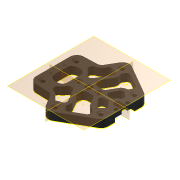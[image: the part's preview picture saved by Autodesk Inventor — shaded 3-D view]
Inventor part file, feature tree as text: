
AUTODESK INVENTOR PART (.ipt)
format: ipt  version: 2016 (Build 200138000, 138)  size: 927,744 bytes
history: native  units: mm
features: sketch x17, extrude x15, plane x3, pattern_circular x3, projected_geometry x3, thread x2, reference x2, chamfer x1, revolve x1, fillet x1
ambient origin geometry x8: Origin, YZ Plane, XZ Plane, XY Plane, X Axis, Y Axis, Z Axis, Center Point
bodies: Solid1 (feature_tree)
feature tree (48):
  extrude  "Extrusion1"  Depth=10.0mm
  extrude  "Extrusion2"  Depth=10.0mm
  extrude  "Extrusion4"  Depth=10.0mm
  chamfer  "Chamfer1"  Distance=8.0mm
  plane  "Work Plane2"
  extrude  "Extrusion10"  Depth=8.0mm TaperAngle=0.0deg
  plane  "Work Plane8"
  extrude  "Extrusion17"  Depth=4.0mm
  extrude  "Extrusion21"  Depth=4.0mm
  extrude  "Extrusion27"  Depth=4.0mm
  extrude  "Extrusion28"  Depth=3.0mm
  extrude  "Extrusion29"  Depth=2.0mm
  plane  "Work Plane10"
  revolve  "Revolution2"  [1 undecoded]
  pattern_circular  "Circular Pattern3"  [2 undecoded]
  thread  "Thread3"  [1 undecoded]
  thread  "Thread4"  [1 undecoded]
  extrude  "Extrusion31"  Depth=4.0mm
  extrude  "Extrusion33"  Depth=10.0mm TaperAngle=0.0deg
  extrude  "Extrusion34"  Depth=8.0mm
  extrude  "Extrusion35"  Depth=8.0mm
  fillet  "Fillet8"  Radius=4.0mm
  extrude  "Extrusion36"  Depth=0.05mm
  extrude  "Extrusion37"  Depth=0.05mm
  pattern_circular  "Circular Pattern6"  [2 undecoded]
  pattern_circular  "Circular Pattern7"  [2 undecoded]
  sketch  "Sketch47"  dims[d133=6.0mm d134=7.5mm d135=8.0mm d136=0.0mm d175=4.0mm d176=4.0mm d177=10.0mm d178=0.0mm d179=8.0mm d180=8.0mm d181=4.0mm d182=0.0mm d183=2.4mm d184=2.4mm d185=8.0mm d186=0.0mm d205=3.5mm d206=10.0mm d207=90.0deg d208=60.0mm d209=360.0deg d211=10.0mm d212=0.0mm d213=10.0mm d214=0.0mm d215=6.0mm d216=6.0mm d217=1.0mm d218=0.0mm d232=8.0mm d233=0.0mm d234=0.349066mm d235=0.349066mm d236=60.0deg d237=60.0deg d238=5.0mm d239=8.0mm d240=0.0mm d243=5.0mm d244=6.0mm d247=3.5mm d248=3.5mm d249=8.0mm d250=8.0mm d251=8.0mm d252=14.0mm d253=8.0mm d254=3.5mm d255=1.75mm d256=6.0mm d260=3.5mm d261=3.5mm d262=3.5mm d263=6.0mm d264=6.0mm d265=6.0mm d266=6.0mm d267=10.0mm d268=10.0mm d269=17.5mm d270=17.5mm d271=3.5mm d272=3.5mm d273=6.0mm d274=6.0mm d275=6.0mm d276=6.0mm d277=3.0mm d279=8.0mm d280=0.0mm d281=3.0mm d282=3.0mm d283=3.0mm d284=0.9mm d285=0.9mm d286=3.6mm d287=3.6mm d288=10.0mm d289=0.0mm d290=10.0mm d291=0.0mm d292=30.0mm d293=360.0deg d295=60.0mm d296=360.0deg d298=0.05mm]
  sketch  "Sketch1"  dims[d1=10.0mm d2=10.0mm]
  reference  "Reference1"
  sketch  "Sketch2"  dims[d3=10.0mm d4=10.0mm]
  reference  "Reference4"
  sketch  "Sketch4"  dims[d5=10.0mm d6=10.0mm d9=8.0mm d10=0.0mm]
  sketch  "Sketch14"  dims[d14=6.5mm d15=8.0mm d16=0.0mm]
  sketch  "Sketch21"  dims[d19=4.0mm d20=4.0mm]
  sketch  "Sketch26"  dims[d21=4.0mm d22=4.0mm]
  sketch  "Sketch34"  dims[d23=4.0mm d24=4.0mm]
  sketch  "Sketch35"  dims[d25=1.5mm d26=0.0mm d31=3.0mm d35=2.2mm d36=2.0mm d37=12.217305mm]
  sketch  "Sketch36"  dims[d55=2.0mm d56=2.0mm]
  sketch  "Sketch38"  dims[d57=2.0mm d58=2.0mm]
  sketch  "Sketch39"  dims[d59=2.0mm]
  sketch  "Sketch41"  dims[d60=2.0mm]
  sketch  "Sketch42"  dims[d61=34.0mm]
  sketch  "Sketch43"  dims[d64=8.2mm]
  sketch  "Sketch45"  dims[d65=5.0mm d66=0.0mm]
  projected_geometry  "Projected Loop2"
  sketch  "Sketch46"  dims[d107=8.0mm d108=0.0mm]
  projected_geometry  "Projected Loop3"
  projected_geometry  "Projected Loop4"
note: 9 required parameter values undecoded (feature->parameter linkage not recoverable at this tier; creation-order binding heuristic only, values carry confidence <= 0.55)